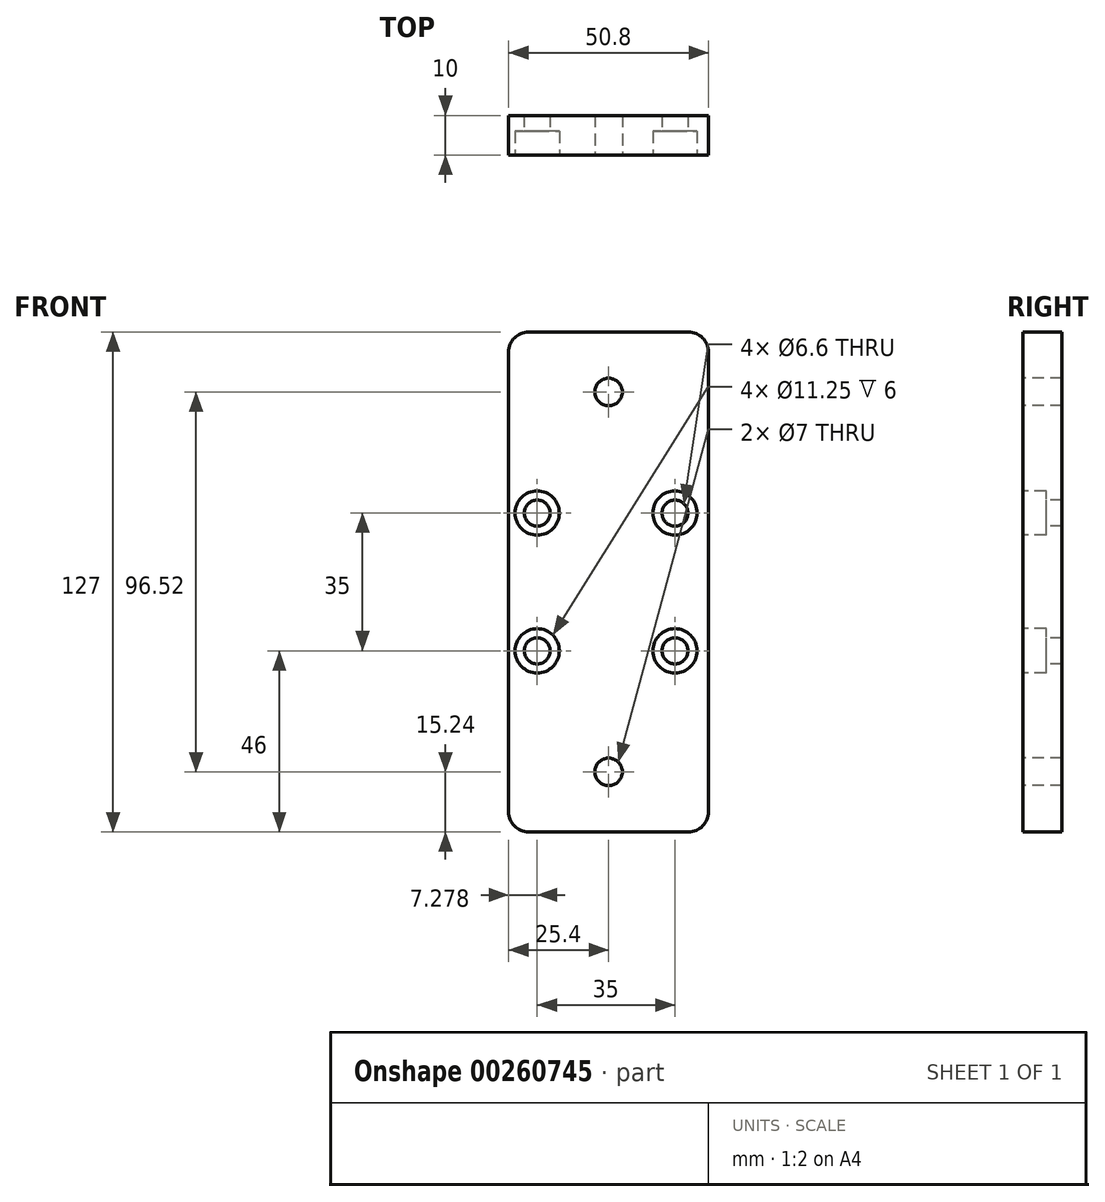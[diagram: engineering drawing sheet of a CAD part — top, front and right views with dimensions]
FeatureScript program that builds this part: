
annotation { "Feature Type Name" : "Feature", "Feature Type Description" : "" }
export const myFeature = defineFeature(function(context is Context, id is Id, definition is map)
    precondition{}
    {
        {
            var Q0;
            Q0=qCreatedBy(makeId("Front.planeOp"),FACE);
            var sketch = newSketch(context, id + "F0", { "sketchPlane" : qUnion([Q0])});
            skLineSegment(sketch, "E0.bottom", {"start": v(25.4, -63.5) * mm, "end": v(-25.4, -63.5) * mm});
            skLineSegment(sketch, "E0.top", {"start": v(25.4, 63.5) * mm, "end": v(-25.4, 63.5) * mm});
            skLineSegment(sketch, "E0.left", {"start": v(25.4, -63.5) * mm, "end": v(25.4, 63.5) * mm});
            skLineSegment(sketch, "E0.right", {"start": v(-25.4, -63.5) * mm, "end": v(-25.4, 63.5) * mm});
            skPoint(sketch, "E0.middle", {"position": v(0, 0) * mm});
            skSolve(sketch);
        }
        {
            var Q0;
            Q0=makeQuery(id+"F0.imprint","IMPRINT",FACE,{"disambiguationData":[TD([[makeQuery(id+"F0.imprint","IMPRINT",EDGE,{"derivedFrom":sQuery(id+"F0.wireOp",EDGE,"E0.bottom")}),-1.0]])]});
            extrude(context, id + "F1", {"entities" : qUnion([Q0]), "depth" : 10 * mm});
        }
        {
            var Q0;
            Q0=makeQuery(id+"F1.opExtrude","SWEPT_EDGE",EDGE,{"disambiguationData":[OSD([sQuery(id+"F0.wireOp",EDGE,"E0.top"),sQuery(id+"F0.wireOp",EDGE,"E0.left")])]});
            var Q1;
            Q1=makeQuery(id+"F1.opExtrude","SWEPT_EDGE",EDGE,{"disambiguationData":[OSD([sQuery(id+"F0.wireOp",EDGE,"E0.bottom"),sQuery(id+"F0.wireOp",EDGE,"E0.left")])]});
            var Q2;
            Q2=makeQuery(id+"F1.opExtrude","SWEPT_EDGE",EDGE,{"disambiguationData":[OSD([sQuery(id+"F0.wireOp",EDGE,"E0.bottom"),sQuery(id+"F0.wireOp",EDGE,"E0.right")])]});
            var Q3;
            Q3=makeQuery(id+"F1.opExtrude","SWEPT_EDGE",EDGE,{"disambiguationData":[OSD([sQuery(id+"F0.wireOp",EDGE,"E0.top"),sQuery(id+"F0.wireOp",EDGE,"E0.right")])]});
            fillet(context, id + "F2", {"entities" : qUnion([Q0, Q1, Q2, Q3]), "radius" : 5.08 * mm, "tangentPropagation" : true, "allowEdgeOverflow" : false});
        }
        {
            var Q0;
            Q0=makeQuery(id+"F1.opExtrude","CAP_FACE",FACE,{"disambiguationData":[OSD([sQuery(id+"F0.wireOp",EDGE,"E0.bottom"),sQuery(id+"F0.wireOp",EDGE,"E0.top"),sQuery(id+"F0.wireOp",EDGE,"E0.left"),sQuery(id+"F0.wireOp",EDGE,"E0.right")])],"isStart":false});
            var sketch = newSketch(context, id + "F3", { "sketchPlane" : qUnion([Q0])});
            skPoint(sketch, "E1", {"position": v(0, 48.26) * mm});
            skPoint(sketch, "E2", {"position": v(0, -48.26) * mm});
            skSolve(sketch);
        }
        {
            var Q0;
            Q0=sQuery(id+"F3.wireOp",VERTEX,"E1");
            var Q1;
            Q1=sQuery(id+"F3.wireOp",VERTEX,"E2");
            var Q2;
            Q2=makeQuery(id+"F1.opExtrude","SWEPT_BODY",BODY,{"disambiguationData":[OSD([sQuery(id+"F0.wireOp",EDGE,"E0.bottom"),sQuery(id+"F0.wireOp",EDGE,"E0.top"),sQuery(id+"F0.wireOp",EDGE,"E0.left"),sQuery(id+"F0.wireOp",EDGE,"E0.right")])]});
            hole(context, id + "F4", {"style" : HoleStyle.SIMPLE, "endStyle" : HoleEndStyle.THROUGH, "standardTappedOrClearance" : lookupTablePath({ "standard" : "ISO", "engagement" : "75%", "pitch" : "1 mm", "size" : "M8", "type" : "Tapped" }), "standardBlindInLast" : lookupTablePath({ "standard" : "ISO", "engagement" : "75%", "pitch" : "1 mm", "size" : "M8", "type" : "Tapped" }), "holeDiameter" : 7 * mm, "showTappedDepth" : true, "tappedDepth" : 12.7 * mm, "tapClearance" : 3, "locations" : qUnion([Q0, Q1]), "scope" : qUnion([Q2]), "majorDiameter" : 8 * mm});
        }
        {
            var Q0;
            Q0=makeQuery(id+"F1.opExtrude","CAP_FACE",FACE,{"disambiguationData":[OSD([sQuery(id+"F0.wireOp",EDGE,"E0.bottom"),sQuery(id+"F0.wireOp",EDGE,"E0.top"),sQuery(id+"F0.wireOp",EDGE,"E0.left"),sQuery(id+"F0.wireOp",EDGE,"E0.right")])],"isStart":false});
            var sketch = newSketch(context, id + "F5", { "sketchPlane" : qUnion([Q0])});
            skPoint(sketch, "E3", {"position": v(-18.12, 17.5) * mm});
            skPoint(sketch, "E4", {"position": v(-18.12, -17.5) * mm});
            skPoint(sketch, "E5", {"position": v(16.88, 17.5) * mm});
            skPoint(sketch, "E6", {"position": v(16.88, -17.5) * mm});
            skSolve(sketch);
        }
        {
            var Q0;
            Q0=sQuery(id+"F5.wireOp",VERTEX,"E3");
            var Q1;
            Q1=sQuery(id+"F5.wireOp",VERTEX,"E5");
            var Q2;
            Q2=sQuery(id+"F5.wireOp",VERTEX,"E6");
            var Q3;
            Q3=sQuery(id+"F5.wireOp",VERTEX,"E4");
            var Q4;
            Q4=makeQuery(id+"F1.opExtrude","SWEPT_BODY",BODY,{"disambiguationData":[OSD([sQuery(id+"F0.wireOp",EDGE,"E0.bottom"),sQuery(id+"F0.wireOp",EDGE,"E0.top"),sQuery(id+"F0.wireOp",EDGE,"E0.left"),sQuery(id+"F0.wireOp",EDGE,"E0.right")])]});
            hole(context, id + "F6", {"style" : HoleStyle.C_BORE, "endStyle" : HoleEndStyle.THROUGH, "standardTappedOrClearance" : lookupTablePath({ "standard" : "ISO", "fit" : "Normal", "size" : "M6", "type" : "Clearance" }), "standardBlindInLast" : lookupTablePath({ "fit" : "Standard", "standard" : "ISO", "size" : "M6", "type" : "Clearance" }), "holeDiameter" : 6.6 * mm, "cBoreDiameter" : 11.25 * mm, "cBoreDepth" : 6 * mm, "tappedDepth" : 12.7 * mm, "tapClearance" : 3, "locations" : qUnion([Q0, Q1, Q2, Q3]), "scope" : qUnion([Q4])});
        }
    });
